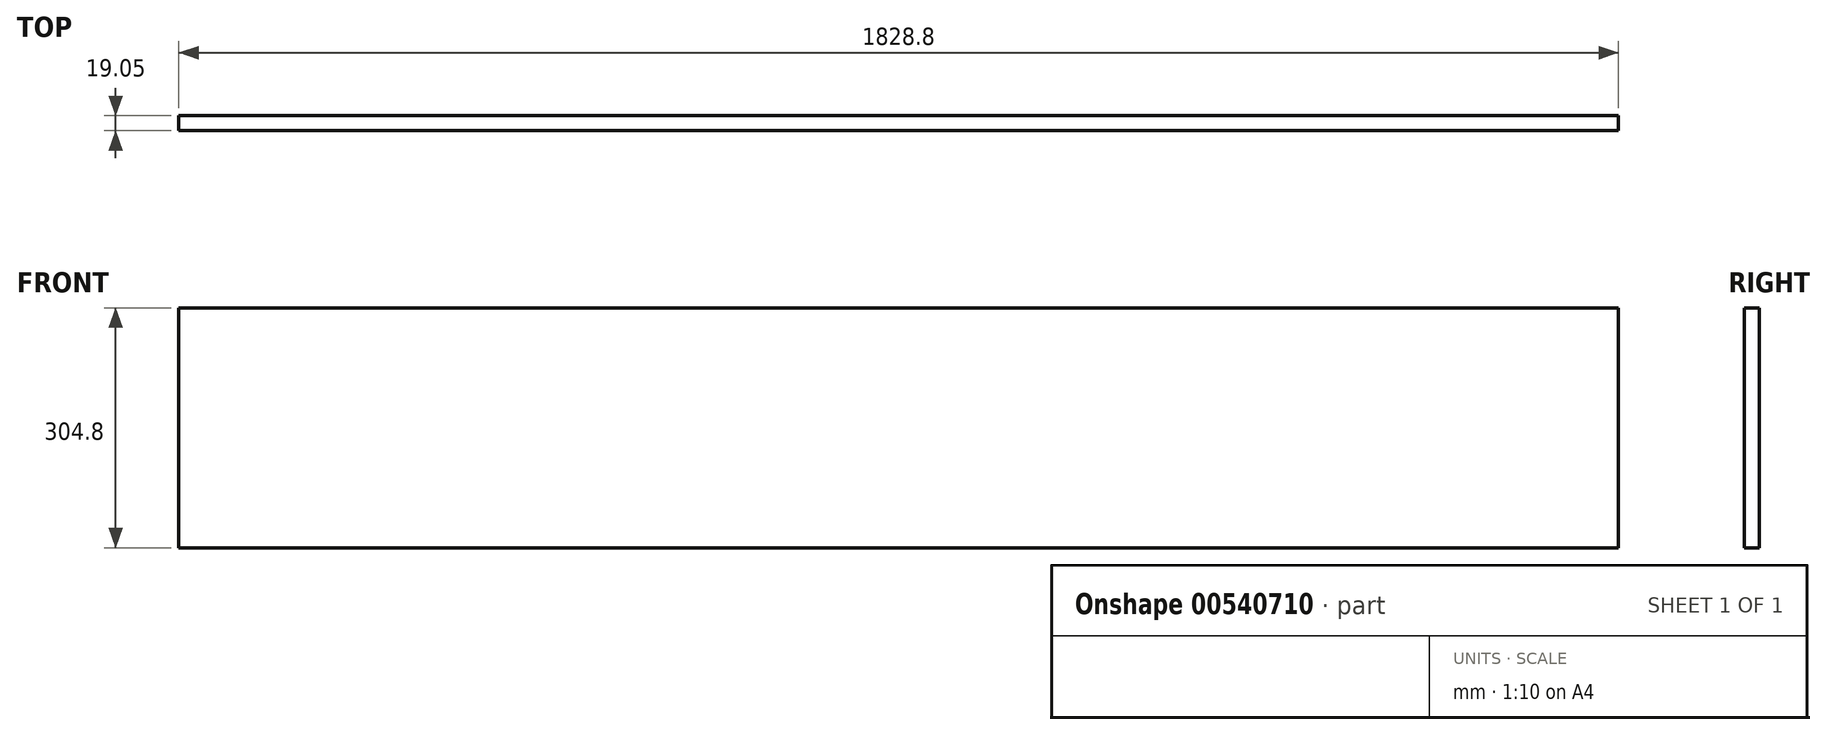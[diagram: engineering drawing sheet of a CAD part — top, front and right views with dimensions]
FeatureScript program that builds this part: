
annotation { "Feature Type Name" : "Feature", "Feature Type Description" : "" }
export const myFeature = defineFeature(function(context is Context, id is Id, definition is map)
    precondition{}
    {
        {
            var Q0;
            Q0=qCreatedBy(makeId("Front.planeOp"),FACE);
            var sketch = newSketch(context, id + "F0", { "sketchPlane" : qUnion([Q0])});
            skLineSegment(sketch, "E0.bottom", {"start": v(914.4, 152.4) * mm, "end": v(-914.4, 152.4) * mm});
            skLineSegment(sketch, "E0.top", {"start": v(914.4, -152.4) * mm, "end": v(-914.4, -152.4) * mm});
            skLineSegment(sketch, "E0.left", {"start": v(914.4, 152.4) * mm, "end": v(914.4, -152.4) * mm});
            skLineSegment(sketch, "E0.right", {"start": v(-914.4, 152.4) * mm, "end": v(-914.4, -152.4) * mm});
            skPoint(sketch, "E0.middle", {"position": v(0, 0) * mm});
            skSolve(sketch);
        }
        {
            var Q0;
            Q0=makeQuery(id+"F0.imprint","IMPRINT",FACE,{"disambiguationData":[TD([[makeQuery(id+"F0.imprint","IMPRINT",EDGE,{"derivedFrom":sQuery(id+"F0.wireOp",EDGE,"E0.bottom")}),1.0]])]});
            extrude(context, id + "F1", {"entities" : qUnion([Q0]), "depth" : 19.05 * mm, "offsetDistance" : 25.4 * mm});
        }
    });
